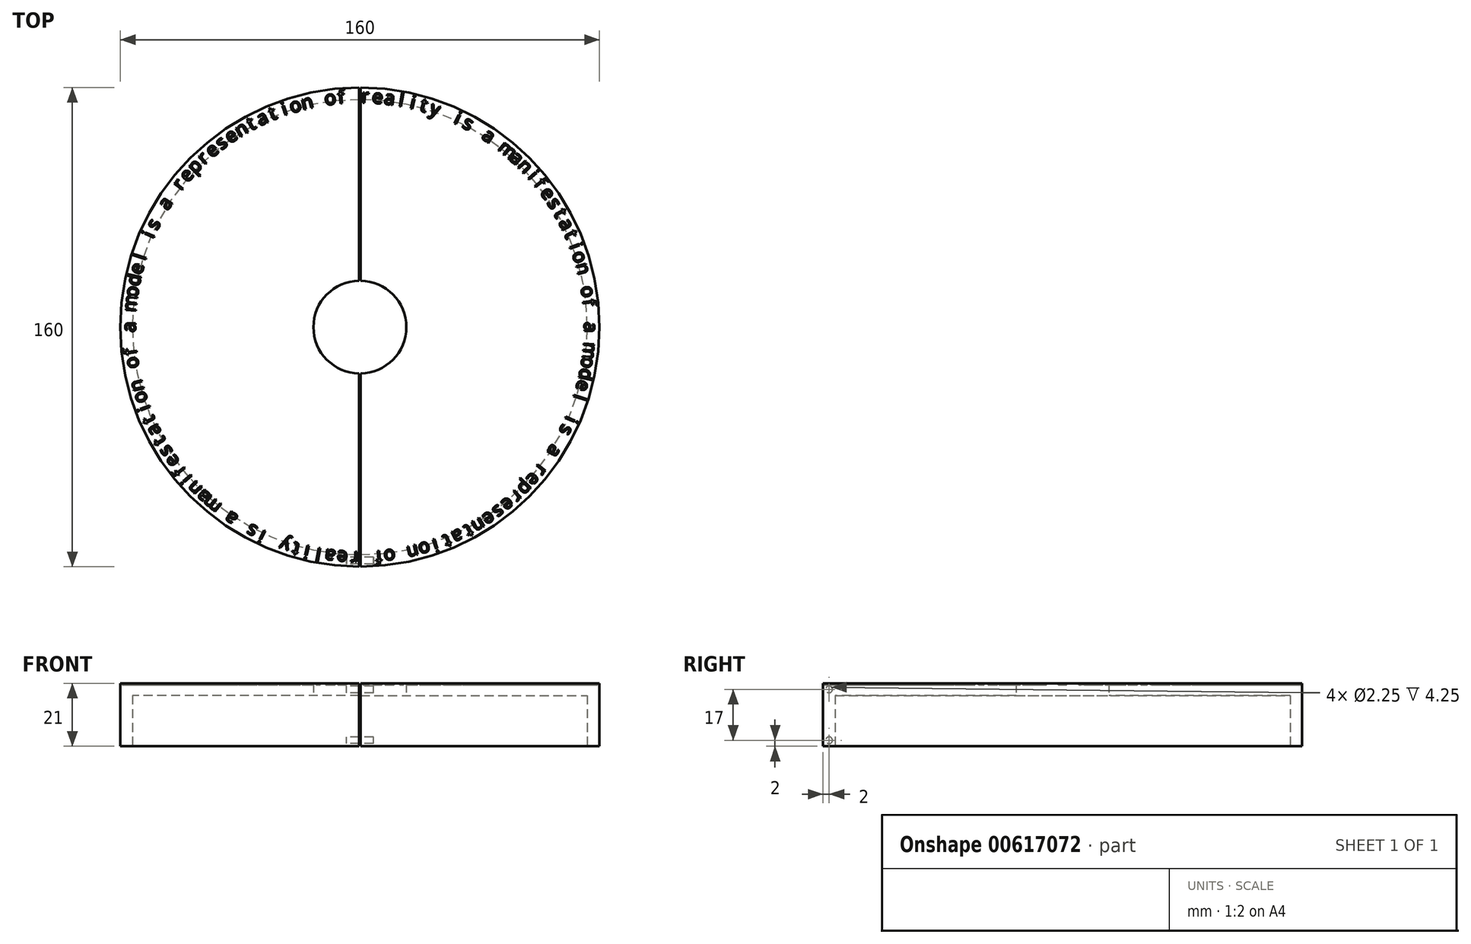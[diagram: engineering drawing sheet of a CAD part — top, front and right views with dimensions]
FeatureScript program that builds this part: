
annotation { "Feature Type Name" : "Feature", "Feature Type Description" : "" }
export const myFeature = defineFeature(function(context is Context, id is Id, definition is map)
    precondition{}
    {
        {
            var Q0;
            Q0=qCreatedBy(makeId("Front.planeOp"),FACE);
            var sketch = newSketch(context, id + "F0", { "sketchPlane" : qUnion([Q0])});
            skLineSegment(sketch, "E0", {"start": v(0, 2) * mm, "end": v(0, 7) * mm});
            skLineSegment(sketch, "E1", {"start": v(-75, 0) * mm, "end": v(-65, 0) * mm});
            skLineSegment(sketch, "E2", {"start": v(-65, 0) * mm, "end": v(-65, 2) * mm});
            skLineSegment(sketch, "E3", {"start": v(-65, 2) * mm, "end": v(0, 2) * mm});
            skLineSegment(sketch, "E4", {"start": v(0, 7) * mm, "end": v(-75, 7) * mm});
            skLineSegment(sketch, "E5", {"start": v(-75, 7) * mm, "end": v(-75, 0) * mm});
            skLineSegment(sketch, "E6.bottom", {"start": v(-15.5, 7) * mm, "end": v(-69.88, 7) * mm});
            skLineSegment(sketch, "E6.top", {"start": v(-15.5, 11) * mm, "end": v(-69.88, 11) * mm});
            skLineSegment(sketch, "E6.left", {"start": v(-15.5, 7) * mm, "end": v(-15.5, 11) * mm});
            skLineSegment(sketch, "E6.right", {"start": v(-69.88, 7) * mm, "end": v(-69.88, 11) * mm});
            skLineSegment(sketch, "E7", {"start": v(-15, 70) * mm, "end": v(-15, 0) * mm});
            skLineSegment(sketch, "E8", {"start": v(-15, 0) * mm, "end": v(15, 0) * mm});
            skLineSegment(sketch, "E9", {"start": v(15, 0) * mm, "end": v(15, 70) * mm});
            skLineSegment(sketch, "E10", {"start": v(15, 70) * mm, "end": v(-15, 70) * mm});
            skLineSegment(sketch, "E11.bottom", {"start": v(-15.5, 12) * mm, "end": v(-71, 12) * mm});
            skLineSegment(sketch, "E11.top", {"start": v(-15.5, 16) * mm, "end": v(-75, 16) * mm});
            skLineSegment(sketch, "E11.left", {"start": v(-15.5, 12) * mm, "end": v(-15.5, 16) * mm});
            skLineSegment(sketch, "E12.top", {"start": v(-75, 7) * mm, "end": v(-71, 7) * mm});
            skLineSegment(sketch, "E12.left", {"start": v(-75, 16) * mm, "end": v(-75, 7) * mm});
            skLineSegment(sketch, "E12.right", {"start": v(-71, 12) * mm, "end": v(-71, 7) * mm});
            skLineSegment(sketch, "E13.bottom", {"start": v(-15.5, 17) * mm, "end": v(-76, 17) * mm});
            skLineSegment(sketch, "E13.top", {"start": v(-15.5, 21) * mm, "end": v(-80, 21) * mm});
            skLineSegment(sketch, "E13.left", {"start": v(-15.5, 17) * mm, "end": v(-15.5, 21) * mm});
            skLineSegment(sketch, "E13.right", {"start": v(-80, 0) * mm, "end": v(-80, 21) * mm});
            skLineSegment(sketch, "E14.bottom", {"start": v(-80, 21) * mm, "end": v(-76, 21) * mm});
            skLineSegment(sketch, "E14.top", {"start": v(-80, 0) * mm, "end": v(-76, 0) * mm});
            skLineSegment(sketch, "E14.right", {"start": v(-76, 17) * mm, "end": v(-76, 0) * mm});
            skSolve(sketch);
        }
        {
            var Q0;
            Q0=makeQuery(id+"F0.imprint","IMPRINT",FACE,{"disambiguationData":[TD([[makeQuery(id+"F0.imprint","IMPRINT",EDGE,{"derivedFrom":sQuery(id+"F0.wireOp",EDGE,"E13.bottom")}),-1.0]])]});
            var Q1;
            Q1=sQuery(id+"F0.wireOp",EDGE,"E0");
            revolve(context, id + "F1", {"entities" : qUnion([Q0]), "axis" : qUnion([Q1]), "revolveType" : RevolveType.FULL});
        }
        {
            var Q0;
            Q0=makeQuery(id+"F1.opRevolve","SWEPT_FACE",FACE,{"disambiguationData":[OSD([sQuery(id+"F0.wireOp",EDGE,"E13.top"),sQuery(id+"F0.wireOp",EDGE,"E14.bottom")])]});
            var sketch = newSketch(context, id + "F2", { "sketchPlane" : qUnion([Q0])});
            skText(sketch, "E15", { "text": "a", "fontName": "OpenSans-Regular.ttf"});
            skLineSegment(sketch, "E16", {"start": v(0, 0) * mm, "end": v(116.2, 0) * mm, "construction": true});
            skLineSegment(sketch, "E17.1.0", {"start": v(0, 0) * mm, "end": v(116.05, 5.98) * mm, "construction": true});
            skLineSegment(sketch, "E17.2.0", {"start": v(0, 0) * mm, "end": v(115.59, 11.95) * mm, "construction": true});
            skLineSegment(sketch, "E17.3.0", {"start": v(0, 0) * mm, "end": v(114.82, 17.88) * mm, "construction": true});
            skLineSegment(sketch, "E17.4.0", {"start": v(0, 0) * mm, "end": v(113.74, 23.77) * mm, "construction": true});
            skLineSegment(sketch, "E17.5.0", {"start": v(0, 0) * mm, "end": v(112.37, 29.6) * mm, "construction": true});
            skLineSegment(sketch, "E17.6.0", {"start": v(0, 0) * mm, "end": v(110.7, 35.34) * mm, "construction": true});
            skLineSegment(sketch, "E17.7.0", {"start": v(0, 0) * mm, "end": v(108.73, 41) * mm, "construction": true});
            skLineSegment(sketch, "E17.8.0", {"start": v(0, 0) * mm, "end": v(106.48, 46.53) * mm, "construction": true});
            skLineSegment(sketch, "E17.9.0", {"start": v(0, 0) * mm, "end": v(103.94, 51.95) * mm, "construction": true});
            skLineSegment(sketch, "E17.10.0", {"start": v(0, 0) * mm, "end": v(101.13, 57.23) * mm, "construction": true});
            skLineSegment(sketch, "E17.11.0", {"start": v(0, 0) * mm, "end": v(98.05, 62.36) * mm, "construction": true});
            skLineSegment(sketch, "E17.12.0", {"start": v(0, 0) * mm, "end": v(94.7, 67.33) * mm, "construction": true});
            skLineSegment(sketch, "E17.13.0", {"start": v(0, 0) * mm, "end": v(91.12, 72.12) * mm, "construction": true});
            skLineSegment(sketch, "E17.14.0", {"start": v(0, 0) * mm, "end": v(87.28, 76.71) * mm, "construction": true});
            skLineSegment(sketch, "E17.15.0", {"start": v(0, 0) * mm, "end": v(83.22, 81.1) * mm, "construction": true});
            skLineSegment(sketch, "E17.16.0", {"start": v(0, 0) * mm, "end": v(78.93, 85.28) * mm, "construction": true});
            skLineSegment(sketch, "E17.17.0", {"start": v(0, 0) * mm, "end": v(74.44, 89.23) * mm, "construction": true});
            skLineSegment(sketch, "E17.18.0", {"start": v(0, 0) * mm, "end": v(69.75, 92.94) * mm, "construction": true});
            skLineSegment(sketch, "E17.19.0", {"start": v(0, 0) * mm, "end": v(64.87, 96.4) * mm, "construction": true});
            skLineSegment(sketch, "E17.20.0", {"start": v(0, 0) * mm, "end": v(59.82, 99.62) * mm, "construction": true});
            skLineSegment(sketch, "E17.21.0", {"start": v(0, 0) * mm, "end": v(54.61, 102.57) * mm, "construction": true});
            skLineSegment(sketch, "E17.22.0", {"start": v(0, 0) * mm, "end": v(49.26, 105.24) * mm, "construction": true});
            skLineSegment(sketch, "E17.23.0", {"start": v(0, 0) * mm, "end": v(43.78, 107.64) * mm, "construction": true});
            skLineSegment(sketch, "E17.24.0", {"start": v(0, 0) * mm, "end": v(38.18, 109.75) * mm, "construction": true});
            skLineSegment(sketch, "E17.25.0", {"start": v(0, 0) * mm, "end": v(32.48, 111.57) * mm, "construction": true});
            skLineSegment(sketch, "E17.26.0", {"start": v(0, 0) * mm, "end": v(26.7, 113.1) * mm, "construction": true});
            skLineSegment(sketch, "E17.27.0", {"start": v(0, 0) * mm, "end": v(20.83, 114.32) * mm, "construction": true});
            skLineSegment(sketch, "E17.28.0", {"start": v(0, 0) * mm, "end": v(14.92, 115.24) * mm, "construction": true});
            skLineSegment(sketch, "E17.29.0", {"start": v(0, 0) * mm, "end": v(8.97, 115.85) * mm, "construction": true});
            skLineSegment(sketch, "E17.30.0", {"start": v(0, 0) * mm, "end": v(3, 116.16) * mm, "construction": true});
            skLineSegment(sketch, "E17.31.0", {"start": v(0, 0) * mm, "end": v(-3, 116.16) * mm, "construction": true});
            skLineSegment(sketch, "E17.32.0", {"start": v(0, 0) * mm, "end": v(-8.97, 115.85) * mm, "construction": true});
            skLineSegment(sketch, "E17.33.0", {"start": v(0, 0) * mm, "end": v(-14.92, 115.24) * mm, "construction": true});
            skLineSegment(sketch, "E17.34.0", {"start": v(0, 0) * mm, "end": v(-20.83, 114.32) * mm, "construction": true});
            skLineSegment(sketch, "E17.35.0", {"start": v(0, 0) * mm, "end": v(-26.7, 113.1) * mm, "construction": true});
            skLineSegment(sketch, "E17.36.0", {"start": v(0, 0) * mm, "end": v(-32.48, 111.57) * mm, "construction": true});
            skLineSegment(sketch, "E17.37.0", {"start": v(0, 0) * mm, "end": v(-38.18, 109.75) * mm, "construction": true});
            skLineSegment(sketch, "E17.38.0", {"start": v(0, 0) * mm, "end": v(-43.78, 107.64) * mm, "construction": true});
            skLineSegment(sketch, "E17.39.0", {"start": v(0, 0) * mm, "end": v(-49.26, 105.24) * mm, "construction": true});
            skLineSegment(sketch, "E17.40.0", {"start": v(0, 0) * mm, "end": v(-54.61, 102.57) * mm, "construction": true});
            skLineSegment(sketch, "E17.41.0", {"start": v(0, 0) * mm, "end": v(-59.82, 99.62) * mm, "construction": true});
            skLineSegment(sketch, "E17.42.0", {"start": v(0, 0) * mm, "end": v(-64.87, 96.4) * mm, "construction": true});
            skLineSegment(sketch, "E17.43.0", {"start": v(0, 0) * mm, "end": v(-69.75, 92.94) * mm, "construction": true});
            skLineSegment(sketch, "E17.44.0", {"start": v(0, 0) * mm, "end": v(-74.44, 89.23) * mm, "construction": true});
            skLineSegment(sketch, "E17.45.0", {"start": v(0, 0) * mm, "end": v(-78.93, 85.28) * mm, "construction": true});
            skLineSegment(sketch, "E17.46.0", {"start": v(0, 0) * mm, "end": v(-83.22, 81.1) * mm, "construction": true});
            skLineSegment(sketch, "E17.47.0", {"start": v(0, 0) * mm, "end": v(-87.28, 76.71) * mm, "construction": true});
            skLineSegment(sketch, "E17.48.0", {"start": v(0, 0) * mm, "end": v(-91.12, 72.12) * mm, "construction": true});
            skLineSegment(sketch, "E17.49.0", {"start": v(0, 0) * mm, "end": v(-94.7, 67.33) * mm, "construction": true});
            skLineSegment(sketch, "E17.50.0", {"start": v(0, 0) * mm, "end": v(-98.05, 62.36) * mm, "construction": true});
            skLineSegment(sketch, "E17.51.0", {"start": v(0, 0) * mm, "end": v(-101.13, 57.23) * mm, "construction": true});
            skLineSegment(sketch, "E17.52.0", {"start": v(0, 0) * mm, "end": v(-103.94, 51.95) * mm, "construction": true});
            skLineSegment(sketch, "E17.53.0", {"start": v(0, 0) * mm, "end": v(-106.48, 46.53) * mm, "construction": true});
            skLineSegment(sketch, "E17.54.0", {"start": v(0, 0) * mm, "end": v(-108.73, 41) * mm, "construction": true});
            skLineSegment(sketch, "E17.55.0", {"start": v(0, 0) * mm, "end": v(-110.7, 35.34) * mm, "construction": true});
            skLineSegment(sketch, "E17.56.0", {"start": v(0, 0) * mm, "end": v(-112.37, 29.6) * mm, "construction": true});
            skLineSegment(sketch, "E17.57.0", {"start": v(0, 0) * mm, "end": v(-113.74, 23.77) * mm, "construction": true});
            skLineSegment(sketch, "E17.58.0", {"start": v(0, 0) * mm, "end": v(-114.82, 17.88) * mm, "construction": true});
            skLineSegment(sketch, "E17.59.0", {"start": v(0, 0) * mm, "end": v(-115.59, 11.95) * mm, "construction": true});
            skLineSegment(sketch, "E17.60.0", {"start": v(0, 0) * mm, "end": v(-116.05, 5.98) * mm, "construction": true});
            skLineSegment(sketch, "E17.61.0", {"start": v(0, 0) * mm, "end": v(-116.2, 0) * mm, "construction": true});
            skLineSegment(sketch, "E17.62.0", {"start": v(0, 0) * mm, "end": v(-116.05, -5.98) * mm, "construction": true});
            skLineSegment(sketch, "E17.63.0", {"start": v(0, 0) * mm, "end": v(-115.59, -11.95) * mm, "construction": true});
            skLineSegment(sketch, "E17.64.0", {"start": v(0, 0) * mm, "end": v(-114.82, -17.88) * mm, "construction": true});
            skLineSegment(sketch, "E17.65.0", {"start": v(0, 0) * mm, "end": v(-113.74, -23.77) * mm, "construction": true});
            skLineSegment(sketch, "E17.66.0", {"start": v(0, 0) * mm, "end": v(-112.37, -29.6) * mm, "construction": true});
            skLineSegment(sketch, "E17.67.0", {"start": v(0, 0) * mm, "end": v(-110.7, -35.34) * mm, "construction": true});
            skLineSegment(sketch, "E17.68.0", {"start": v(0, 0) * mm, "end": v(-108.73, -41) * mm, "construction": true});
            skLineSegment(sketch, "E17.69.0", {"start": v(0, 0) * mm, "end": v(-106.48, -46.53) * mm, "construction": true});
            skLineSegment(sketch, "E17.70.0", {"start": v(0, 0) * mm, "end": v(-103.94, -51.95) * mm, "construction": true});
            skLineSegment(sketch, "E17.71.0", {"start": v(0, 0) * mm, "end": v(-101.13, -57.23) * mm, "construction": true});
            skLineSegment(sketch, "E17.72.0", {"start": v(0, 0) * mm, "end": v(-98.05, -62.36) * mm, "construction": true});
            skLineSegment(sketch, "E17.73.0", {"start": v(0, 0) * mm, "end": v(-94.7, -67.33) * mm, "construction": true});
            skLineSegment(sketch, "E17.74.0", {"start": v(0, 0) * mm, "end": v(-91.12, -72.12) * mm, "construction": true});
            skLineSegment(sketch, "E17.75.0", {"start": v(0, 0) * mm, "end": v(-87.28, -76.71) * mm, "construction": true});
            skLineSegment(sketch, "E17.76.0", {"start": v(0, 0) * mm, "end": v(-83.22, -81.1) * mm, "construction": true});
            skLineSegment(sketch, "E17.77.0", {"start": v(0, 0) * mm, "end": v(-78.93, -85.28) * mm, "construction": true});
            skLineSegment(sketch, "E17.78.0", {"start": v(0, 0) * mm, "end": v(-74.44, -89.23) * mm, "construction": true});
            skLineSegment(sketch, "E17.79.0", {"start": v(0, 0) * mm, "end": v(-69.75, -92.94) * mm, "construction": true});
            skLineSegment(sketch, "E17.80.0", {"start": v(0, 0) * mm, "end": v(-64.87, -96.4) * mm, "construction": true});
            skLineSegment(sketch, "E17.81.0", {"start": v(0, 0) * mm, "end": v(-59.82, -99.62) * mm, "construction": true});
            skLineSegment(sketch, "E17.82.0", {"start": v(0, 0) * mm, "end": v(-54.61, -102.57) * mm, "construction": true});
            skLineSegment(sketch, "E17.83.0", {"start": v(0, 0) * mm, "end": v(-49.26, -105.24) * mm, "construction": true});
            skLineSegment(sketch, "E17.84.0", {"start": v(0, 0) * mm, "end": v(-43.78, -107.64) * mm, "construction": true});
            skLineSegment(sketch, "E17.85.0", {"start": v(0, 0) * mm, "end": v(-38.18, -109.75) * mm, "construction": true});
            skLineSegment(sketch, "E17.86.0", {"start": v(0, 0) * mm, "end": v(-32.48, -111.57) * mm, "construction": true});
            skLineSegment(sketch, "E17.87.0", {"start": v(0, 0) * mm, "end": v(-26.7, -113.1) * mm, "construction": true});
            skLineSegment(sketch, "E17.88.0", {"start": v(0, 0) * mm, "end": v(-20.83, -114.32) * mm, "construction": true});
            skLineSegment(sketch, "E17.89.0", {"start": v(0, 0) * mm, "end": v(-14.92, -115.24) * mm, "construction": true});
            skLineSegment(sketch, "E17.90.0", {"start": v(0, 0) * mm, "end": v(-8.97, -115.85) * mm, "construction": true});
            skLineSegment(sketch, "E17.91.0", {"start": v(0, 0) * mm, "end": v(-3, -116.16) * mm, "construction": true});
            skLineSegment(sketch, "E17.92.0", {"start": v(0, 0) * mm, "end": v(3, -116.16) * mm, "construction": true});
            skLineSegment(sketch, "E17.93.0", {"start": v(0, 0) * mm, "end": v(8.97, -115.85) * mm, "construction": true});
            skLineSegment(sketch, "E17.94.0", {"start": v(0, 0) * mm, "end": v(14.92, -115.24) * mm, "construction": true});
            skLineSegment(sketch, "E17.95.0", {"start": v(0, 0) * mm, "end": v(20.83, -114.32) * mm, "construction": true});
            skLineSegment(sketch, "E17.96.0", {"start": v(0, 0) * mm, "end": v(26.7, -113.1) * mm, "construction": true});
            skLineSegment(sketch, "E17.97.0", {"start": v(0, 0) * mm, "end": v(32.48, -111.57) * mm, "construction": true});
            skLineSegment(sketch, "E17.98.0", {"start": v(0, 0) * mm, "end": v(38.18, -109.75) * mm, "construction": true});
            skLineSegment(sketch, "E17.99.0", {"start": v(0, 0) * mm, "end": v(43.78, -107.64) * mm, "construction": true});
            skLineSegment(sketch, "E17.100.0", {"start": v(0, 0) * mm, "end": v(49.26, -105.24) * mm, "construction": true});
            skLineSegment(sketch, "E17.101.0", {"start": v(0, 0) * mm, "end": v(54.61, -102.57) * mm, "construction": true});
            skLineSegment(sketch, "E17.102.0", {"start": v(0, 0) * mm, "end": v(59.82, -99.62) * mm, "construction": true});
            skLineSegment(sketch, "E17.103.0", {"start": v(0, 0) * mm, "end": v(64.87, -96.4) * mm, "construction": true});
            skLineSegment(sketch, "E17.104.0", {"start": v(0, 0) * mm, "end": v(69.75, -92.94) * mm, "construction": true});
            skLineSegment(sketch, "E17.105.0", {"start": v(0, 0) * mm, "end": v(74.44, -89.23) * mm, "construction": true});
            skLineSegment(sketch, "E17.106.0", {"start": v(0, 0) * mm, "end": v(78.93, -85.28) * mm, "construction": true});
            skLineSegment(sketch, "E17.107.0", {"start": v(0, 0) * mm, "end": v(83.22, -81.1) * mm, "construction": true});
            skLineSegment(sketch, "E17.108.0", {"start": v(0, 0) * mm, "end": v(87.28, -76.71) * mm, "construction": true});
            skLineSegment(sketch, "E17.109.0", {"start": v(0, 0) * mm, "end": v(91.12, -72.12) * mm, "construction": true});
            skLineSegment(sketch, "E17.110.0", {"start": v(0, 0) * mm, "end": v(94.7, -67.33) * mm, "construction": true});
            skLineSegment(sketch, "E17.111.0", {"start": v(0, 0) * mm, "end": v(98.05, -62.36) * mm, "construction": true});
            skLineSegment(sketch, "E17.112.0", {"start": v(0, 0) * mm, "end": v(101.13, -57.23) * mm, "construction": true});
            skLineSegment(sketch, "E17.113.0", {"start": v(0, 0) * mm, "end": v(103.94, -51.95) * mm, "construction": true});
            skLineSegment(sketch, "E17.114.0", {"start": v(0, 0) * mm, "end": v(106.48, -46.53) * mm, "construction": true});
            skLineSegment(sketch, "E17.115.0", {"start": v(0, 0) * mm, "end": v(108.73, -41) * mm, "construction": true});
            skLineSegment(sketch, "E17.116.0", {"start": v(0, 0) * mm, "end": v(110.7, -35.34) * mm, "construction": true});
            skLineSegment(sketch, "E17.117.0", {"start": v(0, 0) * mm, "end": v(112.37, -29.6) * mm, "construction": true});
            skLineSegment(sketch, "E17.118.0", {"start": v(0, 0) * mm, "end": v(113.74, -23.77) * mm, "construction": true});
            skLineSegment(sketch, "E17.119.0", {"start": v(0, 0) * mm, "end": v(114.82, -17.88) * mm, "construction": true});
            skLineSegment(sketch, "E17.120.0", {"start": v(0, 0) * mm, "end": v(115.59, -11.95) * mm, "construction": true});
            skLineSegment(sketch, "E17.121.0", {"start": v(0, 0) * mm, "end": v(116.05, -5.98) * mm, "construction": true});
            skPoint(sketch, "E17.center", {"position": v(0, 0) * mm});
            skCircle(sketch, "E18", {"center": v(0, 0) * mm, "radius": 75 * mm, "construction": true});
            skText(sketch, "E19", { "text": "m", "fontName": "OpenSans-Regular.ttf"});
            skText(sketch, "E20", { "text": "o", "fontName": "OpenSans-Regular.ttf"});
            skText(sketch, "E21", { "text": "d", "fontName": "OpenSans-Regular.ttf"});
            skText(sketch, "E22", { "text": "e", "fontName": "OpenSans-Regular.ttf"});
            skText(sketch, "E23", { "text": "l", "fontName": "OpenSans-Regular.ttf"});
            skText(sketch, "E24", { "text": "i", "fontName": "OpenSans-Regular.ttf"});
            skText(sketch, "E25", { "text": "s", "fontName": "OpenSans-Regular.ttf"});
            skText(sketch, "E26", { "text": "a", "fontName": "OpenSans-Regular.ttf"});
            skText(sketch, "E27", { "text": "o", "fontName": "OpenSans-Regular.ttf"});
            skText(sketch, "E28", { "text": "p", "fontName": "OpenSans-Regular.ttf"});
            skText(sketch, "E29", { "text": "r", "fontName": "OpenSans-Regular.ttf"});
            skText(sketch, "E30", { "text": "e", "fontName": "OpenSans-Regular.ttf"});
            skText(sketch, "E31", { "text": "r", "fontName": "OpenSans-Regular.ttf"});
            skText(sketch, "E32", { "text": "e", "fontName": "OpenSans-Regular.ttf"});
            skText(sketch, "E33", { "text": "s", "fontName": "OpenSans-Regular.ttf"});
            skText(sketch, "E34", { "text": "n", "fontName": "OpenSans-Regular.ttf"});
            skText(sketch, "E35", { "text": "e", "fontName": "OpenSans-Regular.ttf"});
            skText(sketch, "E36", { "text": "t", "fontName": "OpenSans-Regular.ttf"});
            skText(sketch, "E37", { "text": "a", "fontName": "OpenSans-Regular.ttf"});
            skText(sketch, "E38", { "text": "t", "fontName": "OpenSans-Regular.ttf"});
            skText(sketch, "E39", { "text": "i", "fontName": "OpenSans-Regular.ttf"});
            skText(sketch, "E40", { "text": "o", "fontName": "OpenSans-Regular.ttf"});
            skText(sketch, "E41", { "text": "f", "fontName": "OpenSans-Regular.ttf"});
            skText(sketch, "E42", { "text": "n", "fontName": "OpenSans-Regular.ttf"});
            skText(sketch, "E43", { "text": "r", "fontName": "OpenSans-Regular.ttf"});
            skText(sketch, "E44", { "text": "e", "fontName": "OpenSans-Regular.ttf"});
            skText(sketch, "E45", { "text": "a", "fontName": "OpenSans-Regular.ttf"});
            skText(sketch, "E46", { "text": "l", "fontName": "OpenSans-Regular.ttf"});
            skText(sketch, "E47", { "text": "i", "fontName": "OpenSans-Regular.ttf"});
            skText(sketch, "E48", { "text": "t", "fontName": "OpenSans-Regular.ttf"});
            skText(sketch, "E49", { "text": "y", "fontName": "OpenSans-Regular.ttf"});
            skText(sketch, "E50", { "text": "i", "fontName": "OpenSans-Regular.ttf"});
            skText(sketch, "E51", { "text": "s", "fontName": "OpenSans-Regular.ttf"});
            skText(sketch, "E52", { "text": "a", "fontName": "OpenSans-Regular.ttf"});
            skText(sketch, "E53", { "text": "m", "fontName": "OpenSans-Regular.ttf"});
            skText(sketch, "E54", { "text": "a", "fontName": "OpenSans-Regular.ttf"});
            skText(sketch, "E55", { "text": "n", "fontName": "OpenSans-Regular.ttf"});
            skText(sketch, "E56", { "text": "i", "fontName": "OpenSans-Regular.ttf"});
            skText(sketch, "E57", { "text": "f", "fontName": "OpenSans-Regular.ttf"});
            skText(sketch, "E58", { "text": "e", "fontName": "OpenSans-Regular.ttf"});
            skText(sketch, "E59", { "text": "s", "fontName": "OpenSans-Regular.ttf"});
            skText(sketch, "E60", { "text": "t", "fontName": "OpenSans-Regular.ttf"});
            skText(sketch, "E61", { "text": "a", "fontName": "OpenSans-Regular.ttf"});
            skText(sketch, "E62", { "text": "t", "fontName": "OpenSans-Regular.ttf"});
            skText(sketch, "E63", { "text": "i", "fontName": "OpenSans-Regular.ttf"});
            skText(sketch, "E64", { "text": "o", "fontName": "OpenSans-Regular.ttf"});
            skText(sketch, "E65", { "text": "n", "fontName": "OpenSans-Regular.ttf"});
            skText(sketch, "E66", { "text": "o", "fontName": "OpenSans-Regular.ttf"});
            skText(sketch, "E67", { "text": "f", "fontName": "OpenSans-Regular.ttf"});
            skText(sketch, "E68", { "text": "a", "fontName": "OpenSans-Regular.ttf"});
            skText(sketch, "E69", { "text": "m", "fontName": "OpenSans-Regular.ttf"});
            skText(sketch, "E70", { "text": "o", "fontName": "OpenSans-Regular.ttf"});
            skText(sketch, "E71", { "text": "d", "fontName": "OpenSans-Regular.ttf"});
            skText(sketch, "E72", { "text": "e", "fontName": "OpenSans-Regular.ttf"});
            skText(sketch, "E73", { "text": "l", "fontName": "OpenSans-Regular.ttf"});
            skText(sketch, "E74", { "text": "i", "fontName": "OpenSans-Regular.ttf"});
            skText(sketch, "E75", { "text": "s", "fontName": "OpenSans-Regular.ttf"});
            skText(sketch, "E76", { "text": "a", "fontName": "OpenSans-Regular.ttf"});
            skText(sketch, "E77", { "text": "r", "fontName": "OpenSans-Regular.ttf"});
            skText(sketch, "E78", { "text": "e", "fontName": "OpenSans-Regular.ttf"});
            skText(sketch, "E79", { "text": "p", "fontName": "OpenSans-Regular.ttf"});
            skText(sketch, "E80", { "text": "r", "fontName": "OpenSans-Regular.ttf"});
            skText(sketch, "E81", { "text": "e", "fontName": "OpenSans-Regular.ttf"});
            skText(sketch, "E82", { "text": "s", "fontName": "OpenSans-Regular.ttf"});
            skText(sketch, "E83", { "text": "e", "fontName": "OpenSans-Regular.ttf"});
            skText(sketch, "E84", { "text": "n", "fontName": "OpenSans-Regular.ttf"});
            skText(sketch, "E85", { "text": "t", "fontName": "OpenSans-Regular.ttf"});
            skText(sketch, "E86", { "text": "a", "fontName": "OpenSans-Regular.ttf"});
            skText(sketch, "E87", { "text": "t", "fontName": "OpenSans-Regular.ttf"});
            skText(sketch, "E88", { "text": "i", "fontName": "OpenSans-Regular.ttf"});
            skText(sketch, "E89", { "text": "o", "fontName": "OpenSans-Regular.ttf"});
            skText(sketch, "E90", { "text": "n", "fontName": "OpenSans-Regular.ttf"});
            skText(sketch, "E91", { "text": "o", "fontName": "OpenSans-Regular.ttf"});
            skText(sketch, "E92", { "text": "f", "fontName": "OpenSans-Regular.ttf"});
            skText(sketch, "E93", { "text": "r", "fontName": "OpenSans-Regular.ttf"});
            skText(sketch, "E94", { "text": "e", "fontName": "OpenSans-Regular.ttf"});
            skText(sketch, "E95", { "text": "a", "fontName": "OpenSans-Regular.ttf"});
            skText(sketch, "E96", { "text": "l", "fontName": "OpenSans-Regular.ttf"});
            skText(sketch, "E97", { "text": "i", "fontName": "OpenSans-Regular.ttf"});
            skText(sketch, "E98", { "text": "t", "fontName": "OpenSans-Regular.ttf"});
            skText(sketch, "E99", { "text": "y", "fontName": "OpenSans-Regular.ttf"});
            skText(sketch, "E100", { "text": "i", "fontName": "OpenSans-Regular.ttf"});
            skText(sketch, "E101", { "text": "s", "fontName": "OpenSans-Regular.ttf"});
            skText(sketch, "E102", { "text": "a", "fontName": "OpenSans-Regular.ttf"});
            skText(sketch, "E103", { "text": "m", "fontName": "OpenSans-Regular.ttf"});
            skText(sketch, "E104", { "text": "a", "fontName": "OpenSans-Regular.ttf"});
            skText(sketch, "E105", { "text": "n", "fontName": "OpenSans-Regular.ttf"});
            skText(sketch, "E106", { "text": "i", "fontName": "OpenSans-Regular.ttf"});
            skText(sketch, "E107", { "text": "f", "fontName": "OpenSans-Regular.ttf"});
            skText(sketch, "E108", { "text": "e", "fontName": "OpenSans-Regular.ttf"});
            skText(sketch, "E109", { "text": "s", "fontName": "OpenSans-Regular.ttf"});
            skText(sketch, "E110", { "text": "t", "fontName": "OpenSans-Regular.ttf"});
            skText(sketch, "E111", { "text": "a", "fontName": "OpenSans-Regular.ttf"});
            skText(sketch, "E112", { "text": "t", "fontName": "OpenSans-Regular.ttf"});
            skText(sketch, "E113", { "text": "i", "fontName": "OpenSans-Regular.ttf"});
            skText(sketch, "E114", { "text": "o", "fontName": "OpenSans-Regular.ttf"});
            skText(sketch, "E115", { "text": "n", "fontName": "OpenSans-Regular.ttf"});
            skText(sketch, "E116", { "text": "o", "fontName": "OpenSans-Regular.ttf"});
            skText(sketch, "E117", { "text": "f", "fontName": "OpenSans-Regular.ttf"});
            const initialGuessF2  = {"E15": [0.075, 0.00169, 0, -1, 0.0045], "E19": [0.0749, -0.00487, -0.10282, -0.9947, 0.0045], "E20": [0.0744, -0.00965, -0.1539, -0.98809, 0.0045], "E21": [0.0738, -0.01353, -0.20455, -0.97886, 0.0045], "E22": [0.07298, -0.01737, -0.25467, -0.96703, 0.0045], "E23": [0.07167, -0.02212, -0.30411, -0.95264, 0.0045], "E24": [0.06902, -0.02935, -0.40045, -0.91632, 0.0045], "E25": [0.06778, -0.03215, -0.4471, -0.89449, 0.0045], "E26": [0.06419, -0.03883, -0.5367, -0.84378, 0.0045], "E27": [0.01153, -0.07413, -0.99172, -0.1284, 0.0045], "E28": [0.05507, -0.05095, -0.69794, -0.71615, 0.0045], "E29": [0.0597, -0.04542, -0.6206, -0.78412, 0.0045], "E30": [0.05752, -0.04817, -0.66015, -0.75113, 0.0045], "E31": [0.052, -0.05407, -0.73389, -0.67927, 0.0045], "E32": [0.04942, -0.05644, -0.76788, -0.6406, 0.0045], "E33": [0.04626, -0.05906, -0.79984, -0.60021, 0.0045], "E34": [0.04021, -0.06334, -0.85731, -0.5148, 0.0045], "E35": [0.04336, -0.06123, -0.82968, -0.55824, 0.0045], "E36": [0.03634, -0.06562, -0.88268, -0.46998, 0.0045], "E37": [0.03332, -0.06721, -0.9057, -0.42391, 0.0045], "E38": [0.0294, -0.069, -0.92632, -0.37673, 0.0045], "E39": [0.02535, -0.0706, -0.94449, -0.32854, 0.0045], "E40": [0.0228, -0.07148, -0.96015, -0.27949, 0.0045], "E41": [0.00718, -0.07467, -0.99702, -0.07718, 0.0045], "E42": [0.01905, -0.07257, -0.97326, -0.22969, 0.0045], "E43": [-0.0005, -0.07501, -0.99967, 0.02575, 0.0045], "E44": [-0.004, -0.07491, -0.99702, 0.07718, 0.0045], "E45": [-0.00796, -0.0746, -0.99172, 0.1284, 0.0045], "E46": [-0.01273, -0.07391, -0.9838, 0.17928, 0.0045], "E47": [-0.0165, -0.07317, -0.97326, 0.22969, 0.0045], "E48": [-0.01977, -0.07236, -0.96015, 0.27949, 0.0045], "E49": [-0.02296, -0.07142, -0.94449, 0.32854, 0.0045], "E50": [-0.03112, -0.06825, -0.9057, 0.42391, 0.0045], "E51": [-0.03388, -0.06693, -0.88268, 0.46998, 0.0045], "E52": [-0.04047, -0.06317, -0.82968, 0.55824, 0.0045], "E53": [-0.04585, -0.05942, -0.76788, 0.6406, 0.0045], "E54": [-0.0497, -0.05619, -0.73389, 0.67927, 0.0045], "E55": [-0.0524, -0.05368, -0.69794, 0.71615, 0.0045], "E56": [-0.05584, -0.05007, -0.66015, 0.75113, 0.0045], "E57": [-0.05794, -0.04764, -0.6206, 0.78412, 0.0045], "E58": [-0.06009, -0.04492, -0.57942, 0.81503, 0.0045], "E59": [-0.06245, -0.04156, -0.5367, 0.84378, 0.0045], "E60": [-0.06466, -0.03802, -0.49255, 0.87029, 0.0045], "E61": [-0.06633, -0.03504, -0.4471, 0.89449, 0.0045], "E62": [-0.06823, -0.03117, -0.40045, 0.91632, 0.0045], "E63": [-0.06991, -0.02716, -0.35275, 0.93572, 0.0045], "E64": [-0.07087, -0.02463, -0.30411, 0.95264, 0.0045], "E65": [-0.07205, -0.0209, -0.25467, 0.96703, 0.0045], "E66": [-0.07381, -0.01343, -0.1539, 0.98809, 0.0045], "E67": [-0.07446, -0.0091, -0.10282, 0.9947, 0.0045], "E68": [-0.075, -0.00169, 0, 1, 0.0045], "E69": [-0.0749, 0.00487, 0.10282, 0.9947, 0.0045], "E70": [-0.0744, 0.00965, 0.1539, 0.98809, 0.0045], "E71": [-0.0738, 0.01353, 0.20455, 0.97886, 0.0045], "E72": [-0.07298, 0.01737, 0.25467, 0.96703, 0.0045], "E73": [-0.07167, 0.02212, 0.30411, 0.95264, 0.0045], "E74": [-0.06902, 0.02935, 0.40045, 0.91632, 0.0045], "E75": [-0.06778, 0.03215, 0.4471, 0.89449, 0.0045], "E76": [-0.06419, 0.03883, 0.5367, 0.84378, 0.0045], "E77": [-0.0597, 0.04542, 0.6206, 0.78412, 0.0045], "E78": [-0.05752, 0.04817, 0.66015, 0.75113, 0.0045], "E79": [-0.05507, 0.05095, 0.69794, 0.71615, 0.0045], "E80": [-0.052, 0.05407, 0.73389, 0.67927, 0.0045], "E81": [-0.04942, 0.05644, 0.76788, 0.6406, 0.0045], "E82": [-0.04626, 0.05906, 0.79984, 0.60021, 0.0045], "E83": [-0.04336, 0.06123, 0.82968, 0.55824, 0.0045], "E84": [-0.04021, 0.06334, 0.85731, 0.5148, 0.0045], "E85": [-0.03634, 0.06562, 0.88268, 0.46998, 0.0045], "E86": [-0.03332, 0.06721, 0.9057, 0.42391, 0.0045], "E87": [-0.0294, 0.069, 0.92632, 0.37673, 0.0045], "E88": [-0.02535, 0.0706, 0.94449, 0.32854, 0.0045], "E89": [-0.0228, 0.07148, 0.96015, 0.27949, 0.0045], "E90": [-0.01905, 0.07257, 0.97326, 0.22969, 0.0045], "E91": [-0.01153, 0.07413, 0.99172, 0.1284, 0.0045], "E92": [-0.00718, 0.07467, 0.99702, 0.07718, 0.0045], "E93": [0.0005, 0.07501, 0.99967, -0.02575, 0.0045], "E94": [0.004, 0.07491, 0.99702, -0.07718, 0.0045], "E95": [0.00796, 0.0746, 0.99172, -0.1284, 0.0045], "E96": [0.01273, 0.07391, 0.9838, -0.17928, 0.0045], "E97": [0.0165, 0.07317, 0.97326, -0.22969, 0.0045], "E98": [0.01977, 0.07236, 0.96015, -0.27949, 0.0045], "E99": [0.02296, 0.07142, 0.94449, -0.32854, 0.0045], "E100": [0.03112, 0.06825, 0.9057, -0.42391, 0.0045], "E101": [0.03388, 0.06693, 0.88268, -0.46998, 0.0045], "E102": [0.04047, 0.06317, 0.82968, -0.55824, 0.0045], "E103": [0.04585, 0.05942, 0.76788, -0.6406, 0.0045], "E104": [0.0497, 0.05619, 0.73389, -0.67927, 0.0045], "E105": [0.0524, 0.05368, 0.69794, -0.71615, 0.0045], "E106": [0.05584, 0.05007, 0.66015, -0.75113, 0.0045], "E107": [0.05794, 0.04764, 0.6206, -0.78412, 0.0045], "E108": [0.06009, 0.04492, 0.57942, -0.81503, 0.0045], "E109": [0.06245, 0.04156, 0.5367, -0.84378, 0.0045], "E110": [0.06466, 0.03802, 0.49255, -0.87029, 0.0045], "E111": [0.06633, 0.03504, 0.4471, -0.89449, 0.0045], "E112": [0.06823, 0.03117, 0.40045, -0.91632, 0.0045], "E113": [0.06991, 0.02716, 0.35275, -0.93572, 0.0045], "E114": [0.07087, 0.02463, 0.30411, -0.95264, 0.0045], "E115": [0.07205, 0.0209, 0.25467, -0.96703, 0.0045], "E116": [0.07381, 0.01343, 0.1539, -0.98809, 0.0045], "E117": [0.07446, 0.0091, 0.10282, -0.9947, 0.0045]};
            skSetInitialGuess(sketch, initialGuessF2);
            skSolve(sketch);
        }
        {
            var Q0;
            Q0=qSketchRegion(id+"F2",true);
            extrude(context, id + "F3", {"entities" : qUnion([Q0]), "operationType" : NewBodyOperationType.REMOVE, "oppositeDirection" : true, "depth" : 0.5 * mm, "offsetDistance" : 25 * mm});
        }
        {
            var Q0;
            Q0=qCreatedBy(makeId("Top.planeOp"),FACE);
            var sketch = newSketch(context, id + "F4", { "sketchPlane" : qUnion([Q0])});
            skLineSegment(sketch, "E118.bottom", {"start": v(-0.25, 125) * mm, "end": v(0.25, 125) * mm});
            skLineSegment(sketch, "E118.top", {"start": v(-0.25, -125) * mm, "end": v(0.25, -125) * mm});
            skLineSegment(sketch, "E118.left", {"start": v(-0.25, 125) * mm, "end": v(-0.25, -125) * mm});
            skLineSegment(sketch, "E118.right", {"start": v(0.25, 125) * mm, "end": v(0.25, -125) * mm});
            skLineSegment(sketch, "E119", {"start": v(0, 125) * mm, "end": v(0, -125) * mm, "construction": true});
            skLineSegment(sketch, "E120", {"start": v(-0.25, 0) * mm, "end": v(0.25, 0) * mm, "construction": true});
            skSolve(sketch);
        }
        {
            var Q0;
            Q0=qSketchRegion(id+"F4",true);
            extrude(context, id + "F5", {"entities" : qUnion([Q0]), "operationType" : NewBodyOperationType.REMOVE, "endBound" : BoundingType.THROUGH_ALL, "depth" : 25 * mm});
        }
        {
            var Q0;
            Q0=qCreatedBy(makeId("Right.planeOp"),FACE);
            var sketch = newSketch(context, id + "F6", { "sketchPlane" : qUnion([Q0])});
            skCircle(sketch, "E121", {"center": v(-78, 19) * mm, "radius": 1.13 * mm});
            skLineSegment(sketch, "E122", {"start": v(0, 0) * mm, "end": v(0, 19) * mm, "construction": true});
            skLineSegment(sketch, "E123", {"start": v(0, 19) * mm, "end": v(-78, 19) * mm, "construction": true});
            skCircle(sketch, "E124", {"center": v(-78, 2) * mm, "radius": 1.13 * mm});
            skCircle(sketch, "E125.MirrorC", {"center": v(78, 19) * mm, "radius": 1.13 * mm});
            skCircle(sketch, "E126.MirrorC", {"center": v(78, 2) * mm, "radius": 1.13 * mm});
            skSolve(sketch);
        }
        {
            var Q0;
            Q0=makeQuery(id+"F6.imprint","IMPRINT",FACE,{"disambiguationData":[TD([[makeQuery(id+"F6.imprint","IMPRINT",EDGE,{"derivedFrom":sQuery(id+"F6.wireOp",EDGE,"E125.MirrorC")}),-1.0]])]});
            var Q1;
            Q1=makeQuery(id+"F6.imprint","IMPRINT",FACE,{"disambiguationData":[TD([[makeQuery(id+"F6.imprint","IMPRINT",EDGE,{"derivedFrom":sQuery(id+"F6.wireOp",EDGE,"E126.MirrorC")}),-1.0]])]});
            var Q2;
            Q2=makeQuery(id+"F6.imprint","IMPRINT",FACE,{"disambiguationData":[TD([[makeQuery(id+"F6.imprint","IMPRINT",EDGE,{"derivedFrom":sQuery(id+"F6.wireOp",EDGE,"E121")}),1.0]])]});
            var Q3;
            Q3=makeQuery(id+"F6.imprint","IMPRINT",FACE,{"disambiguationData":[TD([[makeQuery(id+"F6.imprint","IMPRINT",EDGE,{"derivedFrom":sQuery(id+"F6.wireOp",EDGE,"E124")}),1.0]])]});
            extrude(context, id + "F7", {"entities" : qUnion([Q0, Q1, Q2, Q3]), "operationType" : NewBodyOperationType.REMOVE, "depth" : 4.5 * mm, "offsetDistance" : 25 * mm, "hasSecondDirection" : true, "secondDirectionOppositeDirection" : true, "secondDirectionDepth" : 4.5 * mm});
        }
    });
